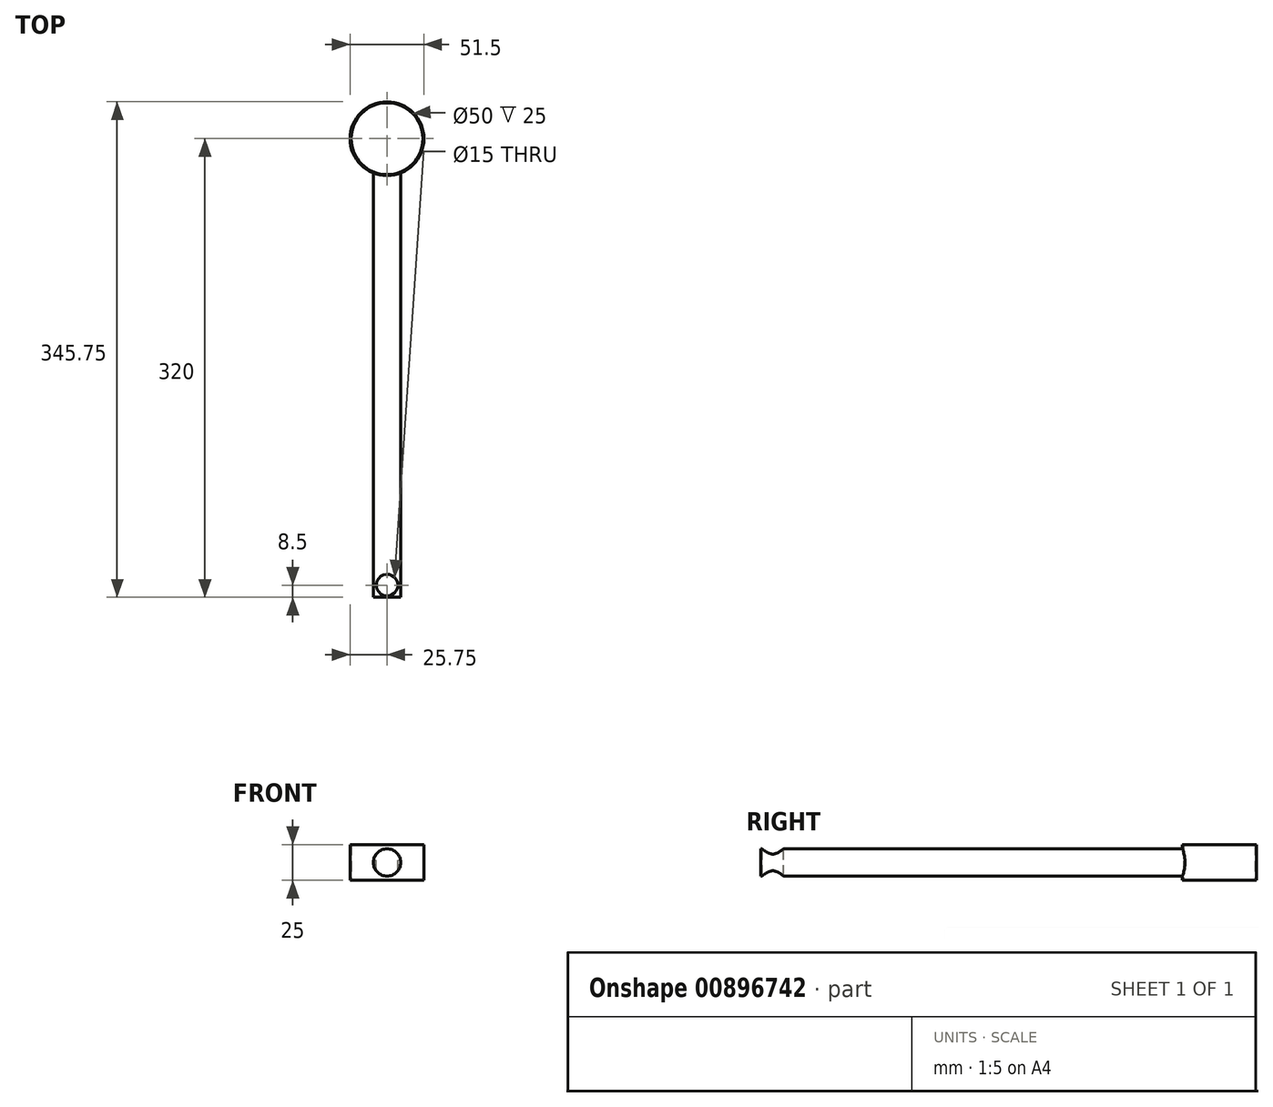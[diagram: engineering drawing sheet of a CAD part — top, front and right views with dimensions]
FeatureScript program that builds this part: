
annotation { "Feature Type Name" : "Feature", "Feature Type Description" : "" }
export const myFeature = defineFeature(function(context is Context, id is Id, definition is map)
    precondition{}
    {
        {
            var Q0;
            Q0=qCreatedBy(makeId("Front.planeOp"),FACE);
            var sketch = newSketch(context, id + "F0", { "sketchPlane" : qUnion([Q0])});
            skCircle(sketch, "E0", {"center": v(0, 0) * mm, "radius": 9.5 * mm});
            skSolve(sketch);
        }
        {
            var Q0;
            Q0=makeQuery(id+"F0.imprint","IMPRINT",FACE,{"disambiguationData":[TD([[makeQuery(id+"F0.imprint","IMPRINT",EDGE,{"derivedFrom":sQuery(id+"F0.wireOp",EDGE,"E0")}),1.0]])]});
            extrude(context, id + "F1", {"entities" : qUnion([Q0]), "oppositeDirection" : true, "depth" : 160 * mm, "offsetDistance" : 25 * mm});
        }
        {
            var Q0;
            Q0=qCreatedBy(makeId("Front.planeOp"),FACE);
            var sketch = newSketch(context, id + "F2", { "sketchPlane" : qUnion([Q0])});
            skLineSegment(sketch, "E1.bottom", {"start": v(18.75, 10) * mm, "end": v(-18.75, 10) * mm});
            skLineSegment(sketch, "E1.top", {"start": v(18.75, -10) * mm, "end": v(-18.75, -10) * mm});
            skLineSegment(sketch, "E1.left", {"start": v(18.75, 10) * mm, "end": v(18.75, -10) * mm});
            skLineSegment(sketch, "E1.right", {"start": v(-18.75, 10) * mm, "end": v(-18.75, -10) * mm});
            skPoint(sketch, "E1.middle", {"position": v(0, 0) * mm});
            skSolve(sketch);
        }
        {
            var Q0;
            Q0=makeQuery(id+"F2.imprint","IMPRINT",FACE,{"disambiguationData":[TD([[makeQuery(id+"F2.imprint","IMPRINT",EDGE,{"derivedFrom":sQuery(id+"F2.wireOp",EDGE,"E1.bottom")}),1.0]])]});
            extrude(context, id + "F3", {"entities" : qUnion([Q0]), "operationType" : NewBodyOperationType.REMOVE, "depth" : 30 * mm, "offsetDistance" : 25 * mm});
        }
        {
            var Q0;
            Q0=qCreatedBy(makeId("Top.planeOp"),FACE);
            var sketch = newSketch(context, id + "F4", { "sketchPlane" : qUnion([Q0])});
            skCircle(sketch, "E2", {"center": v(0, 8.5) * mm, "radius": 7.5 * mm});
            skSolve(sketch);
        }
        {
            var Q0;
            Q0=makeQuery(id+"F4.imprint","IMPRINT",FACE,{"disambiguationData":[TD([[makeQuery(id+"F4.imprint","IMPRINT",EDGE,{"derivedFrom":sQuery(id+"F4.wireOp",EDGE,"E2")}),1.0]])]});
            extrude(context, id + "F5", {"entities" : qUnion([Q0]), "operationType" : NewBodyOperationType.REMOVE, "endBound" : BoundingType.SYMMETRIC, "oppositeDirection" : true, "depth" : 2000 * mm, "offsetDistance" : 25 * mm});
        }
        {
            var Q0;
            Q0=makeQuery(id+"F1.opExtrude","SWEPT_BODY",BODY,{"disambiguationData":[OSD([sQuery(id+"F0.wireOp",EDGE,"E0")])]});
            var Q1;
            Q1=makeQuery(id+"F1.opExtrude","CAP_FACE",FACE,{"disambiguationData":[OSD([sQuery(id+"F0.wireOp",EDGE,"E0")])],"isStart":false});
            mirror(context, id + "F6", {"operationType" : NewBodyOperationType.ADD, "entities" : qUnion([Q0]), "mirrorPlane" : qUnion([Q1])});
        }
        {
            var Q0;
            Q0=qCreatedBy(makeId("Top.planeOp"),FACE);
            var sketch = newSketch(context, id + "F7", { "sketchPlane" : qUnion([Q0])});
            skCircle(sketch, "E3", {"center": v(0, 320) * mm, "radius": 25 * mm});
            skCircle(sketch, "E4", {"center": v(0, 320) * mm, "radius": 25.75 * mm});
            skSolve(sketch);
        }
        {
            var Q0;
            Q0=makeQuery(id+"F7.imprint","IMPRINT",FACE,{"disambiguationData":[TD([[makeQuery(id+"F7.imprint","IMPRINT",EDGE,{"derivedFrom":sQuery(id+"F7.wireOp",EDGE,"E3")}),-1.0]])]});
            extrude(context, id + "F8", {"entities" : qUnion([Q0]), "operationType" : NewBodyOperationType.ADD, "endBound" : BoundingType.SYMMETRIC, "depth" : 25 * mm, "offsetDistance" : 25 * mm});
        }
        {
            var Q0;
            Q0=makeQuery(id+"F7.imprint","IMPRINT",FACE,{"disambiguationData":[TD([[makeQuery(id+"F7.imprint","IMPRINT",EDGE,{"derivedFrom":sQuery(id+"F7.wireOp",EDGE,"E3")}),1.0]])]});
            extrude(context, id + "F9", {"entities" : qUnion([Q0]), "operationType" : NewBodyOperationType.REMOVE, "endBound" : BoundingType.SYMMETRIC, "oppositeDirection" : true, "depth" : 1000 * mm, "offsetDistance" : 25 * mm});
        }
    });
